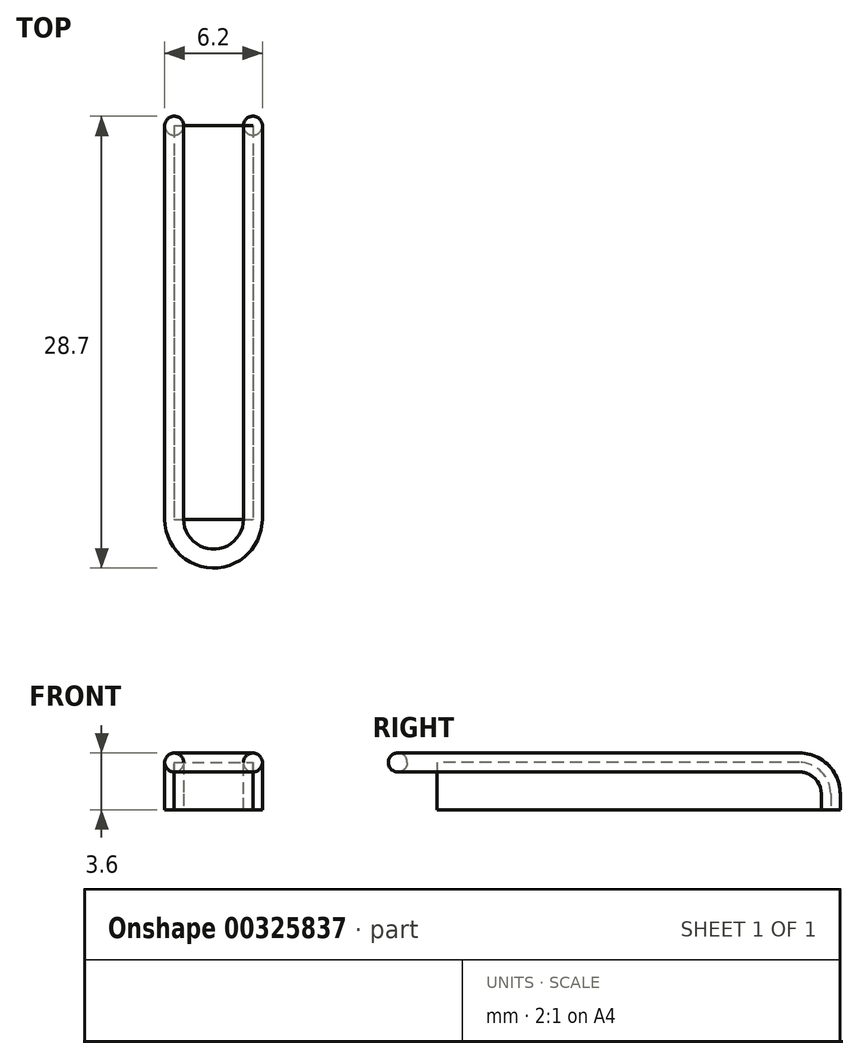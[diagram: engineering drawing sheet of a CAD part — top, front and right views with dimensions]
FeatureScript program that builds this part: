
annotation { "Feature Type Name" : "Feature", "Feature Type Description" : "" }
export const myFeature = defineFeature(function(context is Context, id is Id, definition is map)
    precondition{}
    {
        {
            var Q0;
            Q0=qCreatedBy(makeId("Top.planeOp"),FACE);
            var sketch = newSketch(context, id + "F0", { "sketchPlane" : qUnion([Q0])});
            skLineSegment(sketch, "E0.bottom", {"start": v(-5, -2) * mm, "end": v(0, -2) * mm});
            skLineSegment(sketch, "E0.left", {"start": v(-5, -2) * mm, "end": v(-5, -25) * mm});
            skLineSegment(sketch, "E0.right", {"start": v(0, -2) * mm, "end": v(0, -25) * mm});
            skArc(sketch, "E1", {"start": v(-5, -25) * mm, "mid": v(-2.5, -27.5) * mm, "end": v(0, -25) * mm});
            skSolve(sketch);
        }
        {
            var Q0;
            Q0=qCreatedBy(makeId("Front.planeOp"),FACE);
            var sketch = newSketch(context, id + "F1", { "sketchPlane" : qUnion([Q0])});
            skLineSegment(sketch, "E2.bottom", {"start": v(0, -2) * mm, "end": v(-5, -2) * mm});
            skLineSegment(sketch, "E2.top", {"start": v(0, -3) * mm, "end": v(-5, -3) * mm});
            skLineSegment(sketch, "E2.left", {"start": v(0, -2) * mm, "end": v(0, -3) * mm});
            skLineSegment(sketch, "E2.right", {"start": v(-5, -2) * mm, "end": v(-5, -3) * mm});
            skSolve(sketch);
        }
        {
            var Q0;
            Q0=qCreatedBy(makeId("Right.planeOp"),FACE);
            var sketch = newSketch(context, id + "F2", { "sketchPlane" : qUnion([Q0])});
            skLineSegment(sketch, "E3.bottom", {"start": v(-2, 0) * mm, "end": v(-25, 0) * mm});
            skLineSegment(sketch, "E3.top", {"start": v(0, -3) * mm, "end": v(-25, -3) * mm});
            skLineSegment(sketch, "E3.left", {"start": v(0, -2) * mm, "end": v(0, -3) * mm});
            skLineSegment(sketch, "E3.right", {"start": v(-25, 0) * mm, "end": v(-25, -3) * mm});
            skPoint(sketch, "E4.visualSharp", {"position": v(0, 0) * mm});
            skArc(sketch, "E4.filletArc", {"start": v(0, -2) * mm, "mid": v(-0.59, -0.59) * mm, "end": v(-2, 0) * mm});
            skSolve(sketch);
        }
        {
            var Q0;
            Q0=makeQuery(id+"F2.imprint","IMPRINT",FACE,{"disambiguationData":[TD([[makeQuery(id+"F2.imprint","IMPRINT",EDGE,{"derivedFrom":sQuery(id+"F2.wireOp",EDGE,"E3.bottom")}),1.0]])]});
            extrude(context, id + "F3", {"entities" : qUnion([Q0]), "oppositeDirection" : true, "depth" : 5 * mm});
        }
        {
            var Q0;
            Q0=makeQuery(id+"F3.opExtrude","SWEPT_FACE",FACE,{"disambiguationData":[OSD([sQuery(id+"F2.wireOp",EDGE,"E3.top")])]});
            var sketch = newSketch(context, id + "F4", { "sketchPlane" : qUnion([Q0])});
            skCircle(sketch, "E5", {"center": v(0, 0) * mm, "radius": 0.6 * mm});
            skSolve(sketch);
        }
        {
            var Q0;
            {var subQ0=sQuery(id+"F4.wireOp",EDGE,"E5");var subQ1=sQuery(id+"F2.wireOp",EDGE,"E3.top");var subQ4=makeQuery(id+"F3.opExtrude","CAP_EDGE",EDGE,{"disambiguationData":[OSD([subQ1])],"isStart":true});var subQ5=makeQuery(id+"F4.imprint","INTERSECT",VERTEX,{"derivedFrom":[subQ4,subQ0]});Q0=makeQuery(id+"F4.imprint","IMPRINT",FACE,{"disambiguationData":[TD([[makeQuery(id+"F4.imprint","IMPRINT",EDGE,{"disambiguationData":[TD([[subQ5,1.0]])],"derivedFrom":subQ0}),1.0]])]});}
            var Q1;
            {var subQ0=sQuery(id+"F4.wireOp",EDGE,"E5");var subQ1=sQuery(id+"F2.wireOp",EDGE,"E3.top");var subQ4=makeQuery(id+"F3.opExtrude","CAP_EDGE",EDGE,{"disambiguationData":[OSD([subQ1])],"isStart":true});var subQ5=makeQuery(id+"F4.imprint","INTERSECT",VERTEX,{"derivedFrom":[subQ4,subQ0]});Q1=makeQuery(id+"F4.imprint","IMPRINT",FACE,{"disambiguationData":[TD([[makeQuery(id+"F4.imprint","IMPRINT",EDGE,{"disambiguationData":[TD([[subQ5,-1.0]])],"derivedFrom":subQ0}),1.0]])]});}
            var Q2;
            Q2=sQuery(id+"F1.wireOp",EDGE,"E2.left");
            var Q3;
            Q3=makeQuery(id+"F3.opExtrude","CAP_EDGE",EDGE,{"disambiguationData":[OSD([sQuery(id+"F2.wireOp",EDGE,"E4.filletArc")])],"isStart":true});
            var Q4;
            Q4=sQuery(id+"F0.wireOp",EDGE,"E0.right");
            var Q5;
            Q5=sQuery(id+"F0.wireOp",EDGE,"E1");
            var Q6;
            Q6=sQuery(id+"F0.wireOp",EDGE,"E0.left");
            var Q7;
            Q7=makeQuery(id+"F3.opExtrude","CAP_EDGE",EDGE,{"disambiguationData":[OSD([sQuery(id+"F2.wireOp",EDGE,"E4.filletArc")])],"isStart":false});
            var Q8;
            Q8=sQuery(id+"F1.wireOp",EDGE,"E2.right");
            sweep(context, id + "F5", {"profiles" : qUnion([Q0, Q1]), "path" : qUnion([Q2, Q3, Q4, Q5, Q6, Q7, Q8])});
        }
    });
